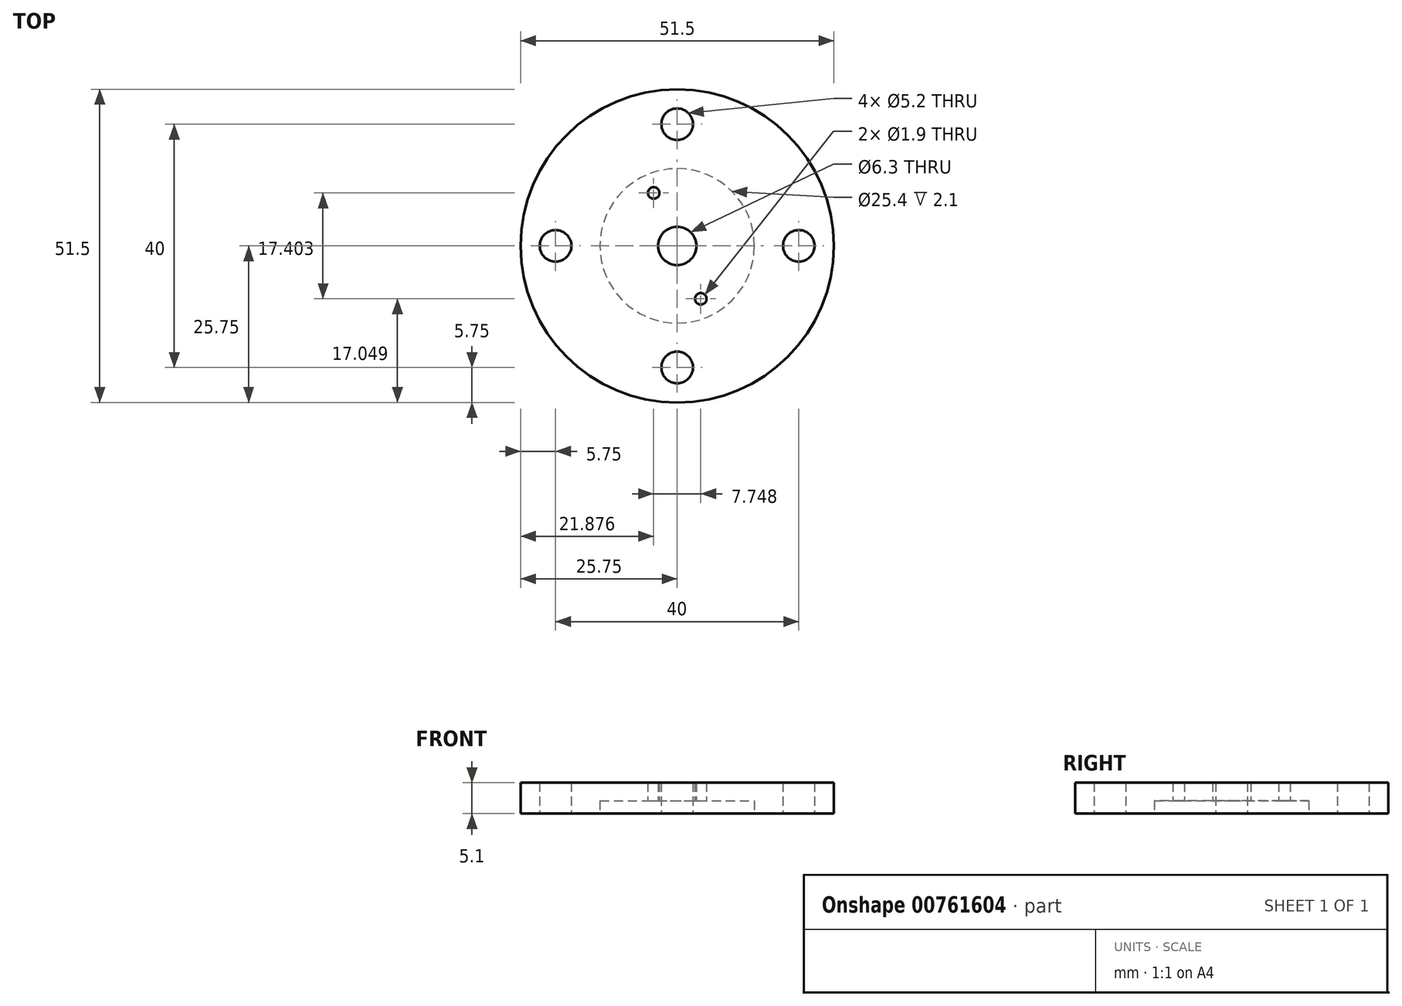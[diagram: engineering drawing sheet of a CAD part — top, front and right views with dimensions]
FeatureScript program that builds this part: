
annotation { "Feature Type Name" : "Feature", "Feature Type Description" : "" }
export const myFeature = defineFeature(function(context is Context, id is Id, definition is map)
    precondition{}
    {
        {
            var Q0;
            Q0=qCreatedBy(makeId("Top.planeOp"),FACE);
            var sketch = newSketch(context, id + "F0", { "sketchPlane" : qUnion([Q0])});
            skCircle(sketch, "E0", {"center": v(0, 0) * mm, "radius": 25.75 * mm});
            skCircle(sketch, "E1", {"center": v(0, 0) * mm, "radius": 20 * mm, "construction": true});
            skCircle(sketch, "E2", {"center": v(0, 20) * mm, "radius": 2.6 * mm});
            skCircle(sketch, "E3.1.0", {"center": v(-20, 0) * mm, "radius": 2.6 * mm});
            skCircle(sketch, "E3.2.0", {"center": v(0, -20) * mm, "radius": 2.6 * mm});
            skCircle(sketch, "E3.3.0", {"center": v(20, 0) * mm, "radius": 2.6 * mm});
            skCircle(sketch, "E4", {"center": v(0, 0) * mm, "radius": 3.15 * mm});
            skCircle(sketch, "E5", {"center": v(0, 0) * mm, "radius": 9.53 * mm, "construction": true});
            skCircle(sketch, "E6", {"center": v(-3.87, 8.7) * mm, "radius": 0.95 * mm});
            skCircle(sketch, "E7", {"center": v(3.87, -8.7) * mm, "radius": 0.95 * mm});
            skLineSegment(sketch, "E8", {"start": v(-3.87, 8.7) * mm, "end": v(3.87, -8.7) * mm, "construction": true});
            skLineSegment(sketch, "E9", {"start": v(0, 0) * mm, "end": v(-23.52, -10.47) * mm, "construction": true});
            skSolve(sketch);
        }
        {
            var Q0;
            Q0 = qSketchRegion(id + "F0", true);
            extrude(context, id + "F1", {"entities" : qUnion([Q0]), "depth" : 5.1 * mm, "offsetDistance" : 25 * mm});
        }
        {
            var Q0;
            Q0=makeQuery(id+"F1.opExtrude","CAP_FACE",FACE,{"disambiguationData":[OSD([sQuery(id+"F0.wireOp",EDGE,"E0"),sQuery(id+"F0.wireOp",EDGE,"E2"),sQuery(id+"F0.wireOp",EDGE,"E3.1.0"),sQuery(id+"F0.wireOp",EDGE,"E3.2.0"),sQuery(id+"F0.wireOp",EDGE,"E3.3.0"),sQuery(id+"F0.wireOp",EDGE,"E4"),sQuery(id+"F0.wireOp",EDGE,"E6"),sQuery(id+"F0.wireOp",EDGE,"E7")])],"isStart":true});
            var sketch = newSketch(context, id + "F2", { "sketchPlane" : qUnion([Q0])});
            skCircle(sketch, "E10", {"center": v(0, 0) * mm, "radius": 12.7 * mm});
            skSolve(sketch);
        }
        {
            var Q0;
            Q0 = qSketchRegion(id + "F2", true);
            extrude(context, id + "F3", {"entities" : qUnion([Q0]), "operationType" : NewBodyOperationType.REMOVE, "oppositeDirection" : true, "depth" : 2.1 * mm, "offsetDistance" : 25 * mm});
        }
    });
